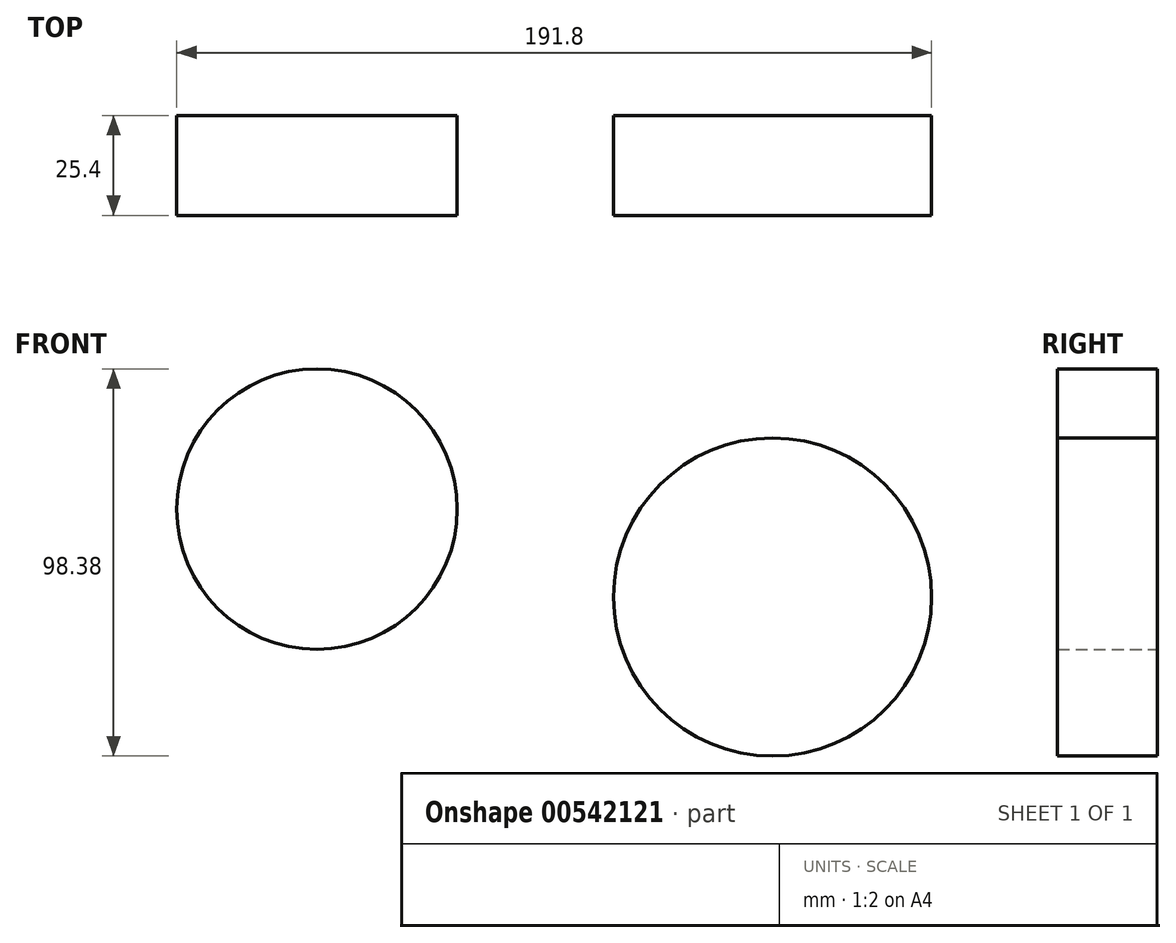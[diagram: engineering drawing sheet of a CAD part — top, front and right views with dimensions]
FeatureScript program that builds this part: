
annotation { "Feature Type Name" : "Feature", "Feature Type Description" : "" }
export const myFeature = defineFeature(function(context is Context, id is Id, definition is map)
    precondition{}
    {
        {
            var Q0;
            Q0=qCreatedBy(makeId("Front.planeOp"),FACE);
            var sketch = newSketch(context, id + "F0", { "sketchPlane" : qUnion([Q0])});
            skCircle(sketch, "E0", {"center": v(-103.6, 14.63) * mm, "radius": 35.63 * mm});
            skCircle(sketch, "E1", {"center": v(12.16, -7.72) * mm, "radius": 40.41 * mm});
            skSolve(sketch);
        }
        {
            var Q0;
            Q0 = qSketchRegion(id + "F0", true);
            extrude(context, id + "F1", {"entities" : qUnion([Q0]), "depth" : 25.4 * mm, "offsetDistance" : 25.4 * mm});
        }
    });
